SOLIDWORKS PART (.sldprt)
format: sldprt  version: not decoded by parser v0  size: 231,424 bytes
history: native  units: mm
features: extrude x6, plane x3, material x1, sketch x1, fillet x1 (+8 scaffold rows collapsed)
feature tree (20):
  scaffold x8  (default folders/planes/origin — collapsed)
  material  "Matériau <non spécifié>"
  plane  "Face"
  plane  "Dessus"
  plane  "Droite"
  sketch  "Esquisse1"  dims[D1=~3.820862mm]
  extrude  "Base-Extrusion"  [1 undecoded]
  extrude  "Esquisse2"  Depth=0.7mm
  extrude  "Boss.-Extru.1"  Depth=0.1mm
  extrude  "Esquisse3"  Depth=0.362225mm
  extrude  "Esquisse11"  Depth=4mm
  extrude  "Boss.-Extru.2"  Depth=0.8mm
  fillet  "Congé1"  Radius=0.35mm
decode coverage: 7 of 8 modeling features carry decoded parameters
note: ~ marks probable driven/reference dimensions
note: 1 parameter value undecoded
note: suppression state not decoded; provenance and decode notes live in map.json
